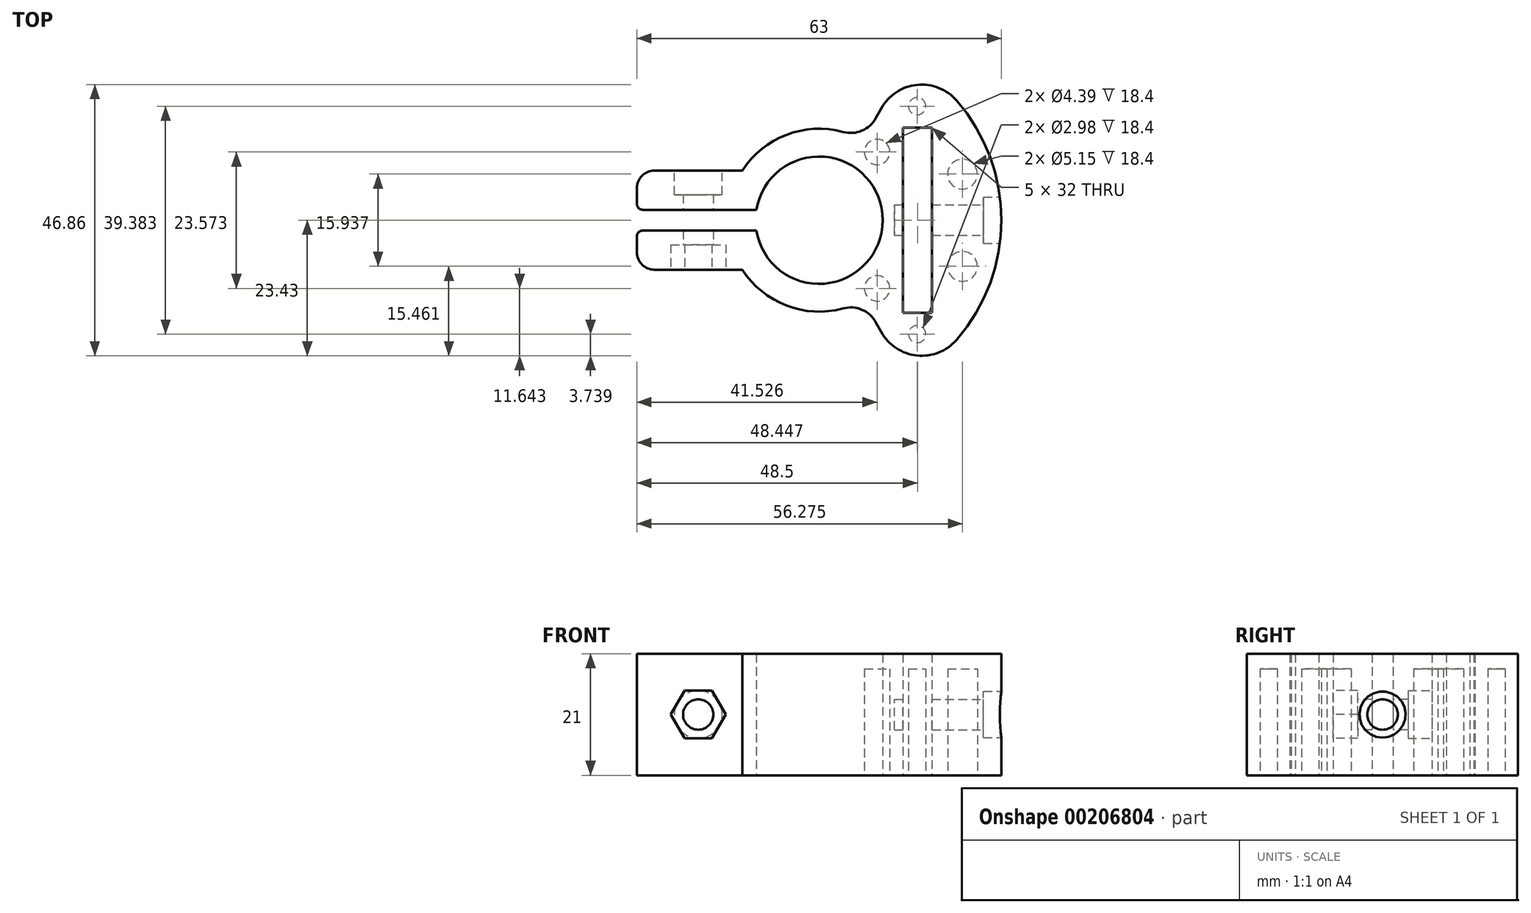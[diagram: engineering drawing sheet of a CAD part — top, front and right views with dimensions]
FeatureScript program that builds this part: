
annotation { "Feature Type Name" : "Feature", "Feature Type Description" : "" }
export const myFeature = defineFeature(function(context is Context, id is Id, definition is map)
    precondition{}
    {
        {
            var Q0;
            Q0=qCreatedBy(makeId("Top.planeOp"),FACE);
            var sketch = newSketch(context, id + "F0", { "sketchPlane" : qUnion([Q0])});
            skArc(sketch, "E0", {"start": v(-10.85, -1.8) * mm, "mid": v(11, 0) * mm, "end": v(-10.85, 1.8) * mm});
            skArc(sketch, "E1", {"start": v(4.13, 15.25) * mm, "mid": v(-8.87, 13.08) * mm, "end": v(-15.7, 1.8) * mm});
            skLineSegment(sketch, "E2", {"start": v(0, 0) * mm, "end": v(14.5, 0) * mm, "construction": true});
            skLineSegment(sketch, "E3.bottom", {"start": v(-31.5, 1.8) * mm, "end": v(-15.7, 1.8) * mm, "construction": true});
            skLineSegment(sketch, "E3.top", {"start": v(-31.5, -1.8) * mm, "end": v(-15.7, -1.8) * mm, "construction": true});
            skLineSegment(sketch, "E3.left", {"start": v(-31.5, 1.8) * mm, "end": v(-31.5, -1.8) * mm, "construction": true});
            skPoint(sketch, "E3.middle", {"position": v(-15.8, 0) * mm});
            skPoint(sketch, "E4", {"position": v(-11, 0) * mm});
            skLineSegment(sketch, "E5", {"start": v(-31.5, 2.8) * mm, "end": v(-31.5, 5.55) * mm});
            skLineSegment(sketch, "E6", {"start": v(-28.5, 8.55) * mm, "end": v(-13.29, 8.55) * mm});
            skLineSegment(sketch, "E7.MirrorCS", {"start": v(-28.5, -8.55) * mm, "end": v(-13.29, -8.55) * mm});
            skLineSegment(sketch, "E8.MirrorCS", {"start": v(-31.5, -2.8) * mm, "end": v(-31.5, -5.55) * mm});
            skLineSegment(sketch, "E9", {"start": v(-30.5, 1.8) * mm, "end": v(-15.7, 1.8) * mm});
            skLineSegment(sketch, "E10", {"start": v(-30.5, -1.8) * mm, "end": v(-15.7, -1.8) * mm});
            skPoint(sketch, "E11.visualSharp", {"position": v(-31.5, 8.55) * mm});
            skArc(sketch, "E11.filletArc", {"start": v(-28.5, 8.55) * mm, "mid": v(-30.62, 7.67) * mm, "end": v(-31.5, 5.55) * mm});
            skPoint(sketch, "E12.visualSharp", {"position": v(-31.5, -8.55) * mm});
            skArc(sketch, "E12.filletArc", {"start": v(-31.5, -5.55) * mm, "mid": v(-30.62, -7.67) * mm, "end": v(-28.5, -8.55) * mm});
            skPoint(sketch, "E13", {"position": v(11, 0) * mm});
            skPoint(sketch, "E14", {"position": v(14.5, 0) * mm});
            skLineSegment(sketch, "E15", {"start": v(14.5, 0) * mm, "end": v(14.5, 16) * mm});
            skLineSegment(sketch, "E16", {"start": v(14.5, 0) * mm, "end": v(14.5, -16) * mm});
            skLineSegment(sketch, "E17.bottom", {"start": v(14.5, 16) * mm, "end": v(19.5, 16) * mm});
            skLineSegment(sketch, "E17.top", {"start": v(14.5, -16) * mm, "end": v(19.5, -16) * mm});
            skLineSegment(sketch, "E17.right", {"start": v(19.5, 16) * mm, "end": v(19.5, -16) * mm});
            skLineSegment(sketch, "E18", {"start": v(9.8, 17.65) * mm, "end": v(10.74, 19.31) * mm});
            skLineSegment(sketch, "E19.MirrorCS", {"start": v(9.8, -17.65) * mm, "end": v(10.74, -19.31) * mm});
            skPoint(sketch, "E20.trimOffspring.end.orphan", {"position": v(31.5, 0) * mm});
            skArc(sketch, "E21.trimOffspring", {"start": v(23.76, -20.68) * mm, "mid": v(31.5, 0) * mm, "end": v(23.76, 20.68) * mm});
            skPoint(sketch, "E22.orphan", {"position": v(-0.1, 1.8) * mm});
            skPoint(sketch, "E23.orphan", {"position": v(-0.1, -1.8) * mm});
            skPoint(sketch, "E24.visualSharp", {"position": v(7.68, 13.8) * mm});
            skArc(sketch, "E24.filletArc", {"start": v(4.13, 15.25) * mm, "mid": v(7.38, 15.47) * mm, "end": v(9.8, 17.65) * mm});
            skPoint(sketch, "E25.visualSharp", {"position": v(7.68, -13.8) * mm});
            skArc(sketch, "E25.filletArc", {"start": v(9.8, -17.65) * mm, "mid": v(7.38, -15.47) * mm, "end": v(4.13, -15.25) * mm});
            skPoint(sketch, "E26.visualSharp", {"position": v(15.3, 27.53) * mm});
            skArc(sketch, "E26.filletArc", {"start": v(23.76, 20.68) * mm, "mid": v(16.9, 23.38) * mm, "end": v(10.74, 19.31) * mm});
            skPoint(sketch, "E27.visualSharp", {"position": v(15.3, -27.53) * mm});
            skArc(sketch, "E27.filletArc", {"start": v(10.74, -19.31) * mm, "mid": v(16.9, -23.38) * mm, "end": v(23.76, -20.68) * mm});
            skPoint(sketch, "E28.visualSharp", {"position": v(-31.5, 1.8) * mm});
            skArc(sketch, "E28.filletArc", {"start": v(-31.5, 2.8) * mm, "mid": v(-31.2, 2.1) * mm, "end": v(-30.5, 1.8) * mm});
            skPoint(sketch, "E29.visualSharp", {"position": v(-31.5, -1.8) * mm});
            skArc(sketch, "E29.filletArc", {"start": v(-30.5, -1.8) * mm, "mid": v(-31.2, -2.1) * mm, "end": v(-31.5, -2.8) * mm});
            skLineSegment(sketch, "E30", {"start": v(-15.7, 1.8) * mm, "end": v(-10.85, 1.8) * mm});
            skLineSegment(sketch, "E31", {"start": v(-15.7, -1.8) * mm, "end": v(-10.85, -1.8) * mm});
            skArc(sketch, "E32.trimOffspring", {"start": v(-15.7, -1.8) * mm, "mid": v(-8.87, -13.08) * mm, "end": v(4.13, -15.25) * mm});
            skSolve(sketch);
        }
        {
            var Q0;
            Q0 = qSketchRegion(id + "F0", true);
            extrude(context, id + "F1", {"entities" : qUnion([Q0]), "depth" : 21 * mm});
        }
        {
            var Q0;
            Q0=makeQuery(id+"F1.opExtrude","SWEPT_FACE",FACE,{"disambiguationData":[OSD([sQuery(id+"F0.wireOp",EDGE,"E7.MirrorCS")])]});
            var sketch = newSketch(context, id + "F2", { "sketchPlane" : qUnion([Q0])});
            skPoint(sketch, "E33", {"position": v(-20.9, 10.5) * mm});
            skPoint(sketch, "E34", {"position": v(-25.64, 10.5) * mm});
            skPoint(sketch, "E35", {"position": v(-16.14, 10.5) * mm});
            skLineSegment(sketch, "E36", {"start": v(-25.64, 10.5) * mm, "end": v(-23.27, 14.61) * mm});
            skLineSegment(sketch, "E37", {"start": v(-23.27, 14.61) * mm, "end": v(-18.52, 14.61) * mm});
            skLineSegment(sketch, "E38", {"start": v(-18.52, 14.61) * mm, "end": v(-16.14, 10.5) * mm});
            skLineSegment(sketch, "E39", {"start": v(-18.52, 6.39) * mm, "end": v(-16.14, 10.5) * mm});
            skLineSegment(sketch, "E40", {"start": v(-23.27, 6.39) * mm, "end": v(-18.52, 6.39) * mm});
            skLineSegment(sketch, "E41", {"start": v(-25.64, 10.5) * mm, "end": v(-23.27, 6.39) * mm});
            skPoint(sketch, "E42.trimOffspring.end.orphan", {"position": v(-13.29, 21) * mm});
            skPoint(sketch, "E43.start.orphan", {"position": v(-28.5, 0) * mm});
            skSolve(sketch);
        }
        {
            var Q0;
            Q0 = qSketchRegion(id + "F2", true);
            extrude(context, id + "F3", {"entities" : qUnion([Q0]), "operationType" : NewBodyOperationType.REMOVE, "oppositeDirection" : true, "depth" : 4.3 * mm});
        }
        {
            var Q0;
            Q0=makeQuery(id+"F3.boolean.opBoolean","COPY",FACE,{"derivedFrom":makeQuery(id+"F3.opExtrude","CAP_FACE",FACE,{"disambiguationData":[OSD([sQuery(id+"F2.wireOp",EDGE,"E36"),sQuery(id+"F2.wireOp",EDGE,"E37"),sQuery(id+"F2.wireOp",EDGE,"E38"),sQuery(id+"F2.wireOp",EDGE,"E39"),sQuery(id+"F2.wireOp",EDGE,"E40"),sQuery(id+"F2.wireOp",EDGE,"E41")])],"isStart":false})});
            var sketch = newSketch(context, id + "F4", { "sketchPlane" : qUnion([Q0])});
            skPoint(sketch, "E44", {"position": v(-20.9, 10.5) * mm});
            skCircle(sketch, "E45", {"center": v(-20.9, 10.5) * mm, "radius": 2.62 * mm});
            skSolve(sketch);
        }
        {
            var Q0;
            Q0 = qSketchRegion(id + "F4", true);
            extrude(context, id + "F5", {"entities" : qUnion([Q0]), "operationType" : NewBodyOperationType.REMOVE, "endBound" : BoundingType.THROUGH_ALL, "oppositeDirection" : true, "depth" : 25 * mm});
        }
        {
            var Q0;
            Q0=makeQuery(id+"F1.opExtrude","SWEPT_FACE",FACE,{"disambiguationData":[OSD([sQuery(id+"F0.wireOp",EDGE,"E6")])]});
            var sketch = newSketch(context, id + "F6", { "sketchPlane" : qUnion([Q0])});
            skCircle(sketch, "E46", {"center": v(20.9, 10.5) * mm, "radius": 4.12 * mm});
            skSolve(sketch);
        }
        {
            var Q0;
            Q0 = qSketchRegion(id + "F6", true);
            extrude(context, id + "F7", {"entities" : qUnion([Q0]), "operationType" : NewBodyOperationType.REMOVE, "oppositeDirection" : true, "depth" : 4.15 * mm});
        }
        {
            var Q0;
            Q0=qCreatedBy(makeId("Right.planeOp"),FACE);
            cPlane(context, id + "F8", {"entities" : qUnion([Q0]), "cplaneType" : CPlaneType.OFFSET, "offset" : 31.5 * mm, "width" : 150 * mm, "height" : 150 * mm});
        }
        {
            var Q0;
            Q0=qCreatedBy(id+"F8.planeOp",FACE);
            var sketch = newSketch(context, id + "F9", { "sketchPlane" : qUnion([Q0])});
            skPoint(sketch, "E47", {"position": v(0, 10.5) * mm});
            skCircle(sketch, "E48", {"center": v(0, 10.5) * mm, "radius": 4 * mm});
            skSolve(sketch);
        }
        {
            var Q0;
            Q0 = qSketchRegion(id + "F9", true);
            extrude(context, id + "F10", {"entities" : qUnion([Q0]), "operationType" : NewBodyOperationType.REMOVE, "oppositeDirection" : true, "depth" : 3.1 * mm});
        }
        {
            var Q0;
            Q0=makeQuery(id+"F10.boolean.opBoolean","COPY",FACE,{"derivedFrom":makeQuery(id+"F10.opExtrude","CAP_FACE",FACE,{"disambiguationData":[OSD([sQuery(id+"F9.wireOp",EDGE,"E48")])],"isStart":false})});
            var sketch = newSketch(context, id + "F11", { "sketchPlane" : qUnion([Q0])});
            skCircle(sketch, "E49", {"center": v(0, 10.5) * mm, "radius": 2.63 * mm});
            skSolve(sketch);
        }
        {
            var Q0;
            Q0 = qSketchRegion(id + "F11", true);
            extrude(context, id + "F12", {"entities" : qUnion([Q0]), "operationType" : NewBodyOperationType.REMOVE, "oppositeDirection" : true, "depth" : 15.4 * mm});
        }
        {
            var Q0;
            Q0=makeQuery(id+"F1.opExtrude","CAP_FACE",FACE,{"disambiguationData":[OSD([sQuery(id+"F0.wireOp",EDGE,"E0"),sQuery(id+"F0.wireOp",EDGE,"E1"),sQuery(id+"F0.wireOp",EDGE,"E5"),sQuery(id+"F0.wireOp",EDGE,"E6"),sQuery(id+"F0.wireOp",EDGE,"E7.MirrorCS"),sQuery(id+"F0.wireOp",EDGE,"E8.MirrorCS"),sQuery(id+"F0.wireOp",EDGE,"E9"),sQuery(id+"F0.wireOp",EDGE,"E10"),sQuery(id+"F0.wireOp",EDGE,"E11.filletArc"),sQuery(id+"F0.wireOp",EDGE,"E12.filletArc"),sQuery(id+"F0.wireOp",EDGE,"E15"),sQuery(id+"F0.wireOp",EDGE,"E16"),sQuery(id+"F0.wireOp",EDGE,"E17.bottom"),sQuery(id+"F0.wireOp",EDGE,"E17.top"),sQuery(id+"F0.wireOp",EDGE,"E17.right"),sQuery(id+"F0.wireOp",EDGE,"E18"),sQuery(id+"F0.wireOp",EDGE,"E19.MirrorCS"),sQuery(id+"F0.wireOp",EDGE,"E21.trimOffspring"),sQuery(id+"F0.wireOp",EDGE,"E24.filletArc"),sQuery(id+"F0.wireOp",EDGE,"E25.filletArc"),sQuery(id+"F0.wireOp",EDGE,"E26.filletArc"),sQuery(id+"F0.wireOp",EDGE,"E27.filletArc"),sQuery(id+"F0.wireOp",EDGE,"E28.filletArc"),sQuery(id+"F0.wireOp",EDGE,"E29.filletArc"),sQuery(id+"F0.wireOp",EDGE,"E30"),sQuery(id+"F0.wireOp",EDGE,"E31"),sQuery(id+"F0.wireOp",EDGE,"E32.trimOffspring")])],"isStart":true});
            var sketch = newSketch(context, id + "F13", { "sketchPlane" : qUnion([Q0])});
            skCircle(sketch, "E50", {"center": v(10.03, 11.79) * mm, "radius": 2.2 * mm});
            skCircle(sketch, "E51.MirrorC", {"center": v(10.03, -11.79) * mm, "radius": 2.2 * mm});
            skCircle(sketch, "E52", {"center": v(24.77, 7.97) * mm, "radius": 2.58 * mm});
            skCircle(sketch, "E53.MirrorC", {"center": v(24.77, -7.97) * mm, "radius": 2.58 * mm});
            skCircle(sketch, "E54", {"center": v(16.95, 19.7) * mm, "radius": 1.5 * mm});
            skCircle(sketch, "E55.MirrorC", {"center": v(16.95, -19.7) * mm, "radius": 1.5 * mm});
            skSolve(sketch);
        }
        {
            var Q0;
            Q0 = qSketchRegion(id + "F13", true);
            extrude(context, id + "F14", {"entities" : qUnion([Q0]), "operationType" : NewBodyOperationType.REMOVE, "oppositeDirection" : true, "depth" : 18.4 * mm});
        }
    });
